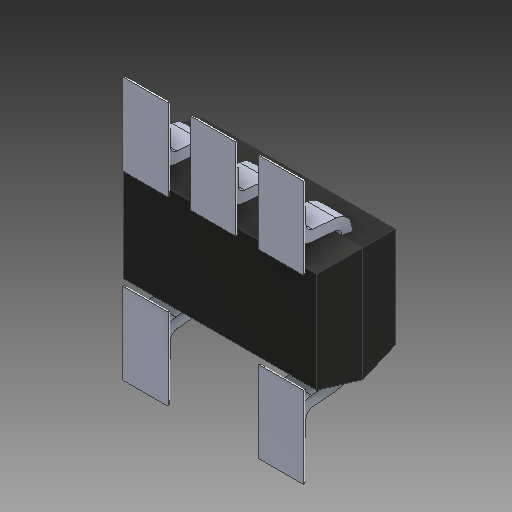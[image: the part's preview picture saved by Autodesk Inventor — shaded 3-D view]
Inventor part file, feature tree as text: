
AUTODESK INVENTOR PART (.ipt)
format: ipt  version: 2018 (Build 220112000, 112)  size: 186,368 bytes
history: native  units: mm
features: fillet x1
ambient origin geometry x8: Origin, YZ Plane, XZ Plane, XY Plane, X Axis, Y Axis, Z Axis, Center Point
bodies: Volumenkörper1 (feature_tree)
feature tree (1):
  fillet  "Fillet2"  [1 undecoded]
note: 1 required parameter value undecoded (feature->parameter linkage not recoverable at this tier; creation-order binding heuristic only, values carry confidence <= 0.55)
